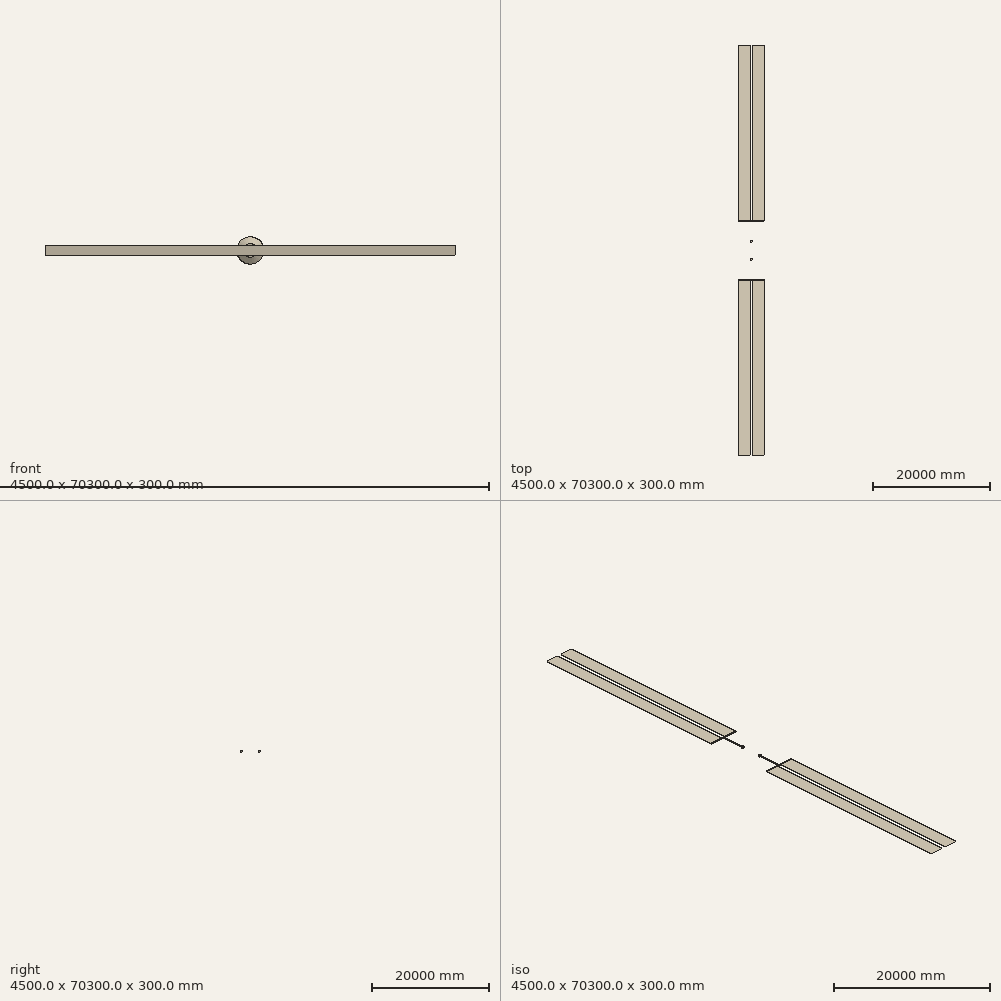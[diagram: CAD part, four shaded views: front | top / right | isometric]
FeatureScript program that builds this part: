
annotation { "Feature Type Name" : "Feature", "Feature Type Description" : "" }
export const myFeature = defineFeature(function(context is Context, id is Id, definition is map)
    precondition{}
    {
        {
            var Q0;
            Q0=qCreatedBy(makeId("Right.planeOp"),FACE);
            var sketch = newSketch(context, id + "F0", { "sketchPlane" : qUnion([Q0])});
            skLineSegment(sketch, "E0", {"start": v(-1700, 975) * mm, "end": v(-1650, 1050) * mm});
            skLineSegment(sketch, "E1", {"start": v(-1650, 1050) * mm, "end": v(-1650, 1000) * mm});
            skLineSegment(sketch, "E2", {"start": v(-1650, 1000) * mm, "end": v(-1400, 1000) * mm});
            skLineSegment(sketch, "E3", {"start": v(-1400, 1000) * mm, "end": v(-1400, 900) * mm});
            skLineSegment(sketch, "E4", {"start": v(-1400, 900) * mm, "end": v(-1700, 900) * mm});
            skLineSegment(sketch, "E5", {"start": v(-1700, 900) * mm, "end": v(-1700, 975) * mm});
            skSolve(sketch);
        }
        {
            var Q0;
            Q0=makeQuery(id+"F0.imprint","IMPRINT",FACE,{"disambiguationData":[TD([[makeQuery(id+"F0.imprint","IMPRINT",EDGE,{"derivedFrom":sQuery(id+"F0.wireOp",EDGE,"E0")}),-1.0]])]});
            var Q1;
            Q1=sQuery(id+"F0.wireOp",EDGE,"E4");
            revolve(context, id + "F1", {"surfaceOperationType" : NewSurfaceOperationType.NEW, "entities" : qUnion([Q0]), "axis" : qUnion([Q1]), "revolveType" : RevolveType.FULL});
        }
        {
            var Q0;
            Q0=makeQuery(id+"F1.opRevolve","SWEPT_FACE",FACE,{"disambiguationData":[OSD([sQuery(id+"F0.wireOp",EDGE,"E5")])]});
            var sketch = newSketch(context, id + "F2", { "sketchPlane" : qUnion([Q0])});
            skLineSegment(sketch, "E6.bottom", {"start": v(-50, 950) * mm, "end": v(50, 950) * mm});
            skLineSegment(sketch, "E6.top", {"start": v(-50, 850) * mm, "end": v(50, 850) * mm});
            skLineSegment(sketch, "E6.left", {"start": v(-50, 950) * mm, "end": v(-50, 850) * mm});
            skLineSegment(sketch, "E6.right", {"start": v(50, 950) * mm, "end": v(50, 850) * mm});
            skLineSegment(sketch, "E7", {"start": v(-50, 900) * mm, "end": v(50, 900) * mm, "construction": true});
            skLineSegment(sketch, "E8", {"start": v(0, 950) * mm, "end": v(0, 850) * mm, "construction": true});
            skSolve(sketch);
        }
        {
            var Q0;
            Q0 = qSketchRegion(id + "F2", true);
            extrude(context, id + "F3", {"entities" : qUnion([Q0]), "operationType" : NewBodyOperationType.ADD, "depth" : 3250 * mm, "offsetDistance" : 25 * mm});
        }
        {
            var Q0;
            Q0=makeQuery(id+"F3.opExtrude","SWEPT_FACE",FACE,{"disambiguationData":[OSD([sQuery(id+"F2.wireOp",EDGE,"E6.bottom")])]});
            var sketch = newSketch(context, id + "F4", { "sketchPlane" : qUnion([Q0])});
            skLineSegment(sketch, "E9.bottom", {"start": v(-2250, -5000) * mm, "end": v(2250, -5000) * mm});
            skLineSegment(sketch, "E9.top", {"start": v(-2250, -5100) * mm, "end": v(2250, -5100) * mm});
            skLineSegment(sketch, "E9.left", {"start": v(-2250, -5000) * mm, "end": v(-2250, -5100) * mm});
            skLineSegment(sketch, "E9.right", {"start": v(2250, -5000) * mm, "end": v(2250, -5100) * mm});
            skSolve(sketch);
        }
        {
            var Q0;
            Q0=makeQuery(id+"F4.imprint","IMPRINT",FACE,{"disambiguationData":[TD([[makeQuery(id+"F4.imprint","IMPRINT",EDGE,{"derivedFrom":sQuery(id+"F4.wireOp",EDGE,"E9.bottom")}),-1.0]])]});
            var Q1;
            Q1=makeQuery(id+"F3.opExtrude","SWEPT_FACE",FACE,{"disambiguationData":[OSD([sQuery(id+"F2.wireOp",EDGE,"E6.top")])]});
            extrude(context, id + "F5", {"entities" : qUnion([Q0]), "endBound" : BoundingType.UP_TO_SURFACE, "oppositeDirection" : true, "depth" : 25 * mm, "endBoundEntityFace" : qUnion([Q1]), "offsetDistance" : 25 * mm});
        }
        {
            var Q0;
            Q0=makeQuery(id+"F5.opExtrude","CAP_FACE",FACE,{"disambiguationData":[OSD([sQuery(id+"F4.wireOp",EDGE,"E9.bottom"),sQuery(id+"F4.wireOp",EDGE,"E9.top"),sQuery(id+"F4.wireOp",EDGE,"E9.left"),sQuery(id+"F4.wireOp",EDGE,"E9.right")])],"isStart":true});
            cPlane(context, id + "F6", {"entities" : qUnion([Q0]), "cplaneType" : CPlaneType.OFFSET, "offset" : 50 * mm, "oppositeDirection" : true, "width" : 150 * mm, "height" : 150 * mm});
        }
        {
            var Q0;
            Q0=qCreatedBy(id+"F6.planeOp",FACE);
            var sketch = newSketch(context, id + "F7", { "sketchPlane" : qUnion([Q0])});
            skLineSegment(sketch, "E10.bottom", {"start": v(-2250, -35150) * mm, "end": v(-250, -35150) * mm});
            skLineSegment(sketch, "E10.top", {"start": v(-2250, -5150) * mm, "end": v(-250, -5150) * mm});
            skLineSegment(sketch, "E10.left", {"start": v(-2250, -35150) * mm, "end": v(-2250, -5150) * mm});
            skLineSegment(sketch, "E10.right", {"start": v(-250, -35150) * mm, "end": v(-250, -5150) * mm});
            skLineSegment(sketch, "E11.bottom", {"start": v(250, -35150) * mm, "end": v(2250, -35150) * mm});
            skLineSegment(sketch, "E11.top", {"start": v(250, -5150) * mm, "end": v(2250, -5150) * mm});
            skLineSegment(sketch, "E11.left", {"start": v(250, -35150) * mm, "end": v(250, -5150) * mm});
            skLineSegment(sketch, "E11.right", {"start": v(2250, -35150) * mm, "end": v(2250, -5150) * mm});
            skSolve(sketch);
        }
        {
            var Q0;
            Q0 = qSketchRegion(id + "F7", true);
            extrude(context, id + "F8", {"entities" : qUnion([Q0]), "endBound" : BoundingType.SYMMETRIC, "depth" : 5 * mm, "offsetDistance" : 25 * mm});
        }
        {
            var Q0;
            Q0=makeQuery(id+"F1.opRevolve","SWEPT_BODY",BODY,{"disambiguationData":[OSD([sQuery(id+"F0.wireOp",EDGE,"E0"),sQuery(id+"F0.wireOp",EDGE,"E1"),sQuery(id+"F0.wireOp",EDGE,"E2"),sQuery(id+"F0.wireOp",EDGE,"E3"),sQuery(id+"F0.wireOp",EDGE,"E4"),sQuery(id+"F0.wireOp",EDGE,"E5")])]});
            var Q1;
            Q1=makeQuery(id+"F5.opExtrude","SWEPT_BODY",BODY,{"disambiguationData":[OSD([sQuery(id+"F4.wireOp",EDGE,"E9.bottom"),sQuery(id+"F4.wireOp",EDGE,"E9.top"),sQuery(id+"F4.wireOp",EDGE,"E9.left"),sQuery(id+"F4.wireOp",EDGE,"E9.right")])]});
            var Q2;
            Q2=makeQuery(id+"F8.opExtrude","SWEPT_BODY",BODY,{"disambiguationData":[OSD([sQuery(id+"F7.wireOp",EDGE,"E10.bottom"),sQuery(id+"F7.wireOp",EDGE,"E10.top"),sQuery(id+"F7.wireOp",EDGE,"E10.left"),sQuery(id+"F7.wireOp",EDGE,"E10.right")])]});
            var Q3;
            Q3=makeQuery(id+"F8.opExtrude","SWEPT_BODY",BODY,{"disambiguationData":[OSD([sQuery(id+"F7.wireOp",EDGE,"E11.bottom"),sQuery(id+"F7.wireOp",EDGE,"E11.top"),sQuery(id+"F7.wireOp",EDGE,"E11.left"),sQuery(id+"F7.wireOp",EDGE,"E11.right")])]});
            var Q4;
            Q4=qCreatedBy(makeId("Front.planeOp"),FACE);
            mirror(context, id + "F9", {"operationType" : NewBodyOperationType.ADD, "entities" : qUnion([Q0, Q1, Q2, Q3]), "mirrorPlane" : qUnion([Q4])});
        }
    });
